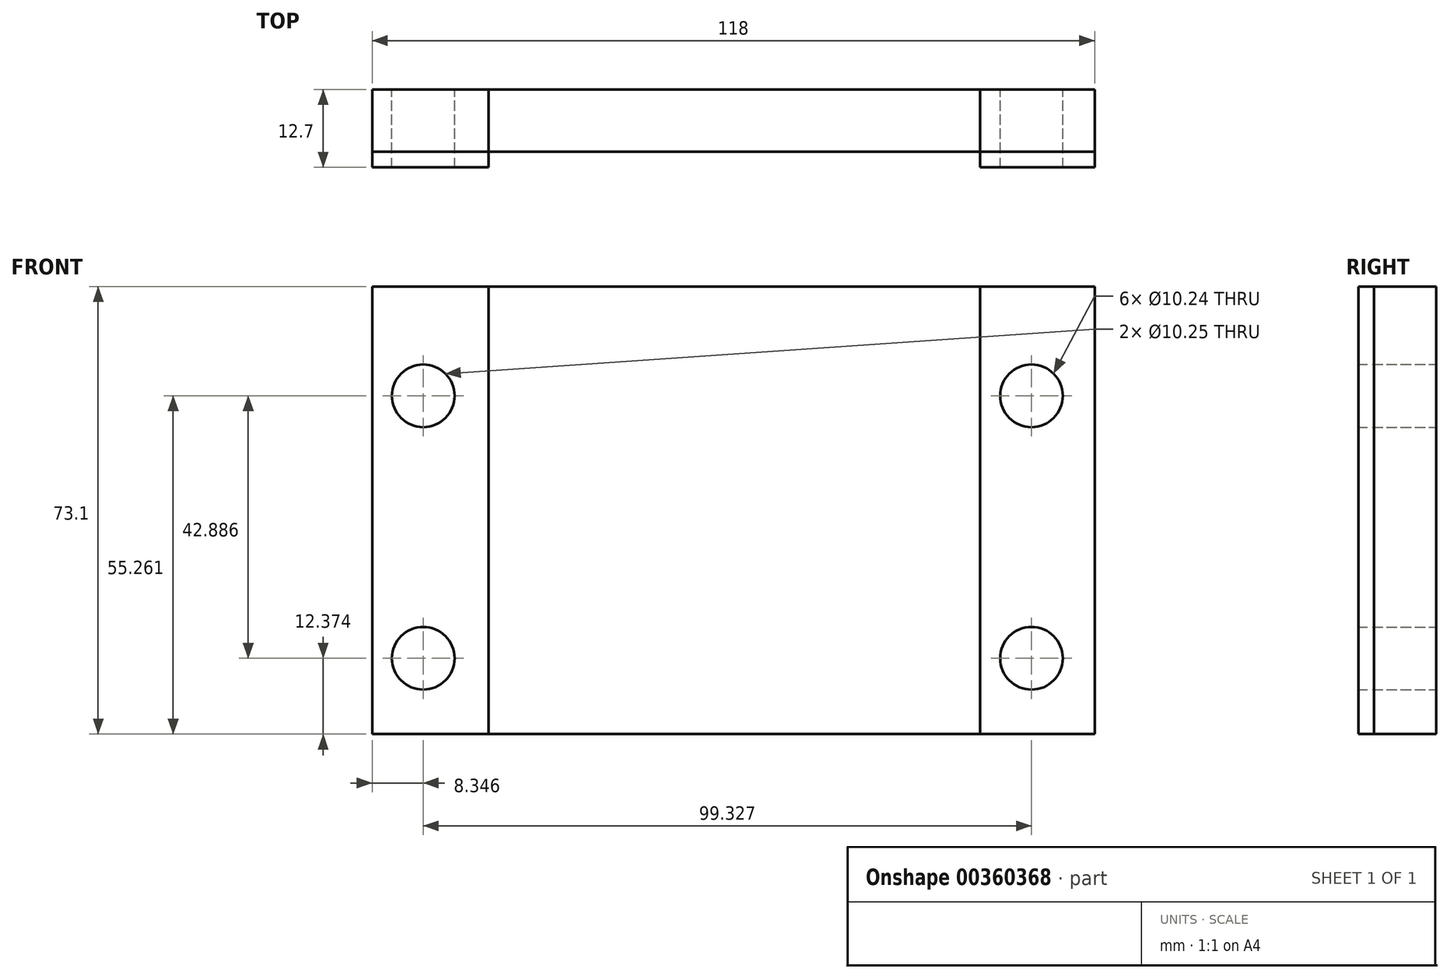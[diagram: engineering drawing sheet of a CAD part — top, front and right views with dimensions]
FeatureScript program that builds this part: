
annotation { "Feature Type Name" : "Feature", "Feature Type Description" : "" }
export const myFeature = defineFeature(function(context is Context, id is Id, definition is map)
    precondition{}
    {
        {
            var Q0;
            Q0=qCreatedBy(makeId("Front.planeOp"),FACE);
            var sketch = newSketch(context, id + "F0", { "sketchPlane" : qUnion([Q0])});
            skLineSegment(sketch, "E0.bottom", {"start": v(59, 36.55) * mm, "end": v(-59, 36.55) * mm});
            skLineSegment(sketch, "E0.top", {"start": v(59, -36.55) * mm, "end": v(-59, -36.55) * mm});
            skLineSegment(sketch, "E0.left", {"start": v(59, 36.55) * mm, "end": v(59, -36.55) * mm});
            skLineSegment(sketch, "E0.right", {"start": v(-59, 36.55) * mm, "end": v(-59, -36.55) * mm});
            skPoint(sketch, "E0.middle", {"position": v(0, 0) * mm});
            skLineSegment(sketch, "E1", {"start": v(-40, 36.55) * mm, "end": v(-40, -36.55) * mm});
            skLineSegment(sketch, "E2", {"start": v(40.3, 36.55) * mm, "end": v(40.3, -36.55) * mm});
            skCircle(sketch, "E3", {"center": v(-50.65, 18.71) * mm, "radius": 5.12 * mm});
            skCircle(sketch, "E4", {"center": v(-50.65, -24.18) * mm, "radius": 5.12 * mm});
            skCircle(sketch, "E5", {"center": v(48.67, 18.71) * mm, "radius": 5.12 * mm});
            skCircle(sketch, "E6", {"center": v(48.67, -24.18) * mm, "radius": 5.12 * mm});
            skSolve(sketch);
        }
        {
            var Q0;
            {var subQ1=sQuery(id+"F0.wireOp",EDGE,"E0.right");Q0=makeQuery(id+"F0.imprint","IMPRINT",FACE,{"disambiguationData":[TD([[makeQuery(id+"F0.imprint","IMPRINT",EDGE,{"derivedFrom":subQ1}),1.0]])]});}
            var Q1;
            {var subQ1=sQuery(id+"F0.wireOp",EDGE,"E0.left");Q1=makeQuery(id+"F0.imprint","IMPRINT",FACE,{"disambiguationData":[TD([[makeQuery(id+"F0.imprint","IMPRINT",EDGE,{"derivedFrom":subQ1}),-1.0]])]});}
            extrude(context, id + "F1", {"entities" : qUnion([Q0, Q1]), "depth" : 12.7 * mm});
        }
        {
            var Q0;
            Q0 = qSketchRegion(id + "F0", true);
            extrude(context, id + "F2", {"entities" : qUnion([Q0]), "depth" : 10.16 * mm});
        }
    });
